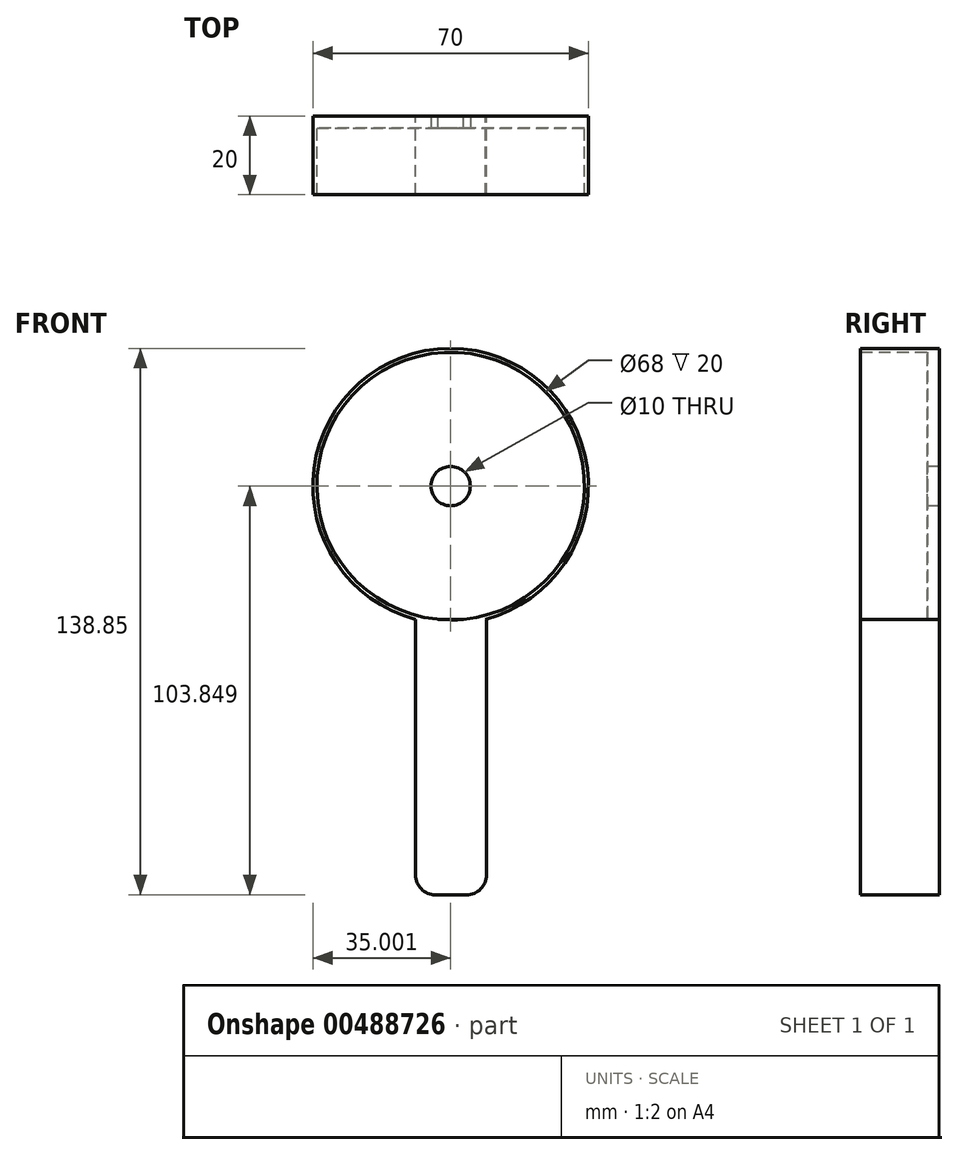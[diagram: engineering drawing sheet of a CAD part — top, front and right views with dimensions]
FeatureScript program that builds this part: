
annotation { "Feature Type Name" : "Feature", "Feature Type Description" : "" }
export const myFeature = defineFeature(function(context is Context, id is Id, definition is map)
    precondition{}
    {
        {
            var Q0;
            Q0=qCreatedBy(makeId("Front.planeOp"),FACE);
            var sketch = newSketch(context, id + "F0", { "sketchPlane" : qUnion([Q0])});
            skCircle(sketch, "E0", {"center": v(-51.15, 34.8) * mm, "radius": 35 * mm});
            skCircle(sketch, "E1", {"center": v(-51.15, 34.8) * mm, "radius": 34 * mm});
            skLineSegment(sketch, "E2.bottom", {"start": v(-60.06, 0.95) * mm, "end": v(-42.06, 0.95) * mm});
            skLineSegment(sketch, "E2.top", {"start": v(-55.06, -69.05) * mm, "end": v(-47.06, -69.05) * mm});
            skLineSegment(sketch, "E2.left", {"start": v(-60.06, 0.95) * mm, "end": v(-60.06, -64.05) * mm});
            skLineSegment(sketch, "E2.right", {"start": v(-42.06, 0.95) * mm, "end": v(-42.06, -64.05) * mm});
            skPoint(sketch, "E3.visualSharp", {"position": v(-42.06, -69.05) * mm});
            skArc(sketch, "E3.filletArc", {"start": v(-47.06, -69.05) * mm, "mid": v(-43.53, -67.58) * mm, "end": v(-42.06, -64.05) * mm});
            skPoint(sketch, "E4.visualSharp", {"position": v(-60.06, -69.05) * mm});
            skArc(sketch, "E4.filletArc", {"start": v(-60.06, -64.05) * mm, "mid": v(-58.6, -67.58) * mm, "end": v(-55.06, -69.05) * mm});
            skSolve(sketch);
        }
        {
            var Q0;
            {var subQ0=sQuery(id+"F0.wireOp",EDGE,"E2.bottom");var subQ4=sQuery(id+"F0.wireOp",EDGE,"E1");var subQ6=makeQuery(id+"F0.imprint","INTERSECT",VERTEX,{"disambiguationData":[OD(0.0)],"derivedFrom":[subQ4,subQ0]});Q0=makeQuery(id+"F0.imprint","IMPRINT",FACE,{"disambiguationData":[TD([[makeQuery(id+"F0.imprint","IMPRINT",EDGE,{"disambiguationData":[TD([[subQ6,1.0]])],"derivedFrom":subQ4}),-1.0]])]});}
            extrude(context, id + "F1", {"entities" : qUnion([Q0]), "depth" : 20 * mm});
        }
        {
            var Q0;
            Q0=makeQuery(id+"F0.imprint","IMPRINT",FACE,{"disambiguationData":[TD([[makeQuery(id+"F0.imprint","IMPRINT",EDGE,{"derivedFrom":sQuery(id+"F0.wireOp",EDGE,"E2.top")}),1.0]])]});
            var Q1;
            {var subQ0=sQuery(id+"F0.wireOp",EDGE,"E2.bottom");var subQ4=sQuery(id+"F0.wireOp",EDGE,"E1");var subQ5=makeQuery(id+"F0.imprint","INTERSECT",VERTEX,{"disambiguationData":[OD(0.0)],"derivedFrom":[subQ4,subQ0]});Q1=makeQuery(id+"F0.imprint","IMPRINT",FACE,{"disambiguationData":[TD([[makeQuery(id+"F0.imprint","IMPRINT",EDGE,{"disambiguationData":[TD([[subQ5,-1.0]])],"derivedFrom":subQ4}),-1.0]])]});}
            extrude(context, id + "F2", {"entities" : qUnion([Q0, Q1]), "operationType" : NewBodyOperationType.ADD, "depth" : 20 * mm});
        }
        {
            var Q0;
            {var subQ0=sQuery(id+"F0.wireOp",EDGE,"E2.bottom");var subQ1=sQuery(id+"F0.wireOp",EDGE,"E1");var subQ2=makeQuery(id+"F0.imprint","INTERSECT",VERTEX,{"disambiguationData":[OD(0.0)],"derivedFrom":[subQ1,subQ0]});Q0=makeQuery(id+"F0.imprint","IMPRINT",FACE,{"disambiguationData":[TD([[makeQuery(id+"F0.imprint","IMPRINT",EDGE,{"disambiguationData":[TD([[subQ2,1.0]])],"derivedFrom":subQ1}),1.0]])]});}
            extrude(context, id + "F3", {"entities" : qUnion([Q0]), "operationType" : NewBodyOperationType.ADD, "depth" : 3 * mm});
        }
        {
            var Q0;
            Q0=makeQuery(id+"F3.opExtrude","CAP_FACE",FACE,{"disambiguationData":[OSD([sQuery(id+"F0.wireOp",EDGE,"E1"),sQuery(id+"F0.wireOp",EDGE,"E2.bottom")])],"isStart":false});
            var sketch = newSketch(context, id + "F4", { "sketchPlane" : qUnion([Q0])});
            skCircle(sketch, "E5", {"center": v(-51.15, 34.8) * mm, "radius": 5 * mm});
            skSolve(sketch);
        }
        {
            var Q0;
            Q0=makeQuery(id+"F4.imprint","IMPRINT",FACE,{"disambiguationData":[TD([[makeQuery(id+"F4.imprint","IMPRINT",EDGE,{"derivedFrom":sQuery(id+"F4.wireOp",EDGE,"E5")}),1.0]])]});
            extrude(context, id + "F5", {"entities" : qUnion([Q0]), "operationType" : NewBodyOperationType.REMOVE, "oppositeDirection" : true, "depth" : 100 * mm});
        }
    });
